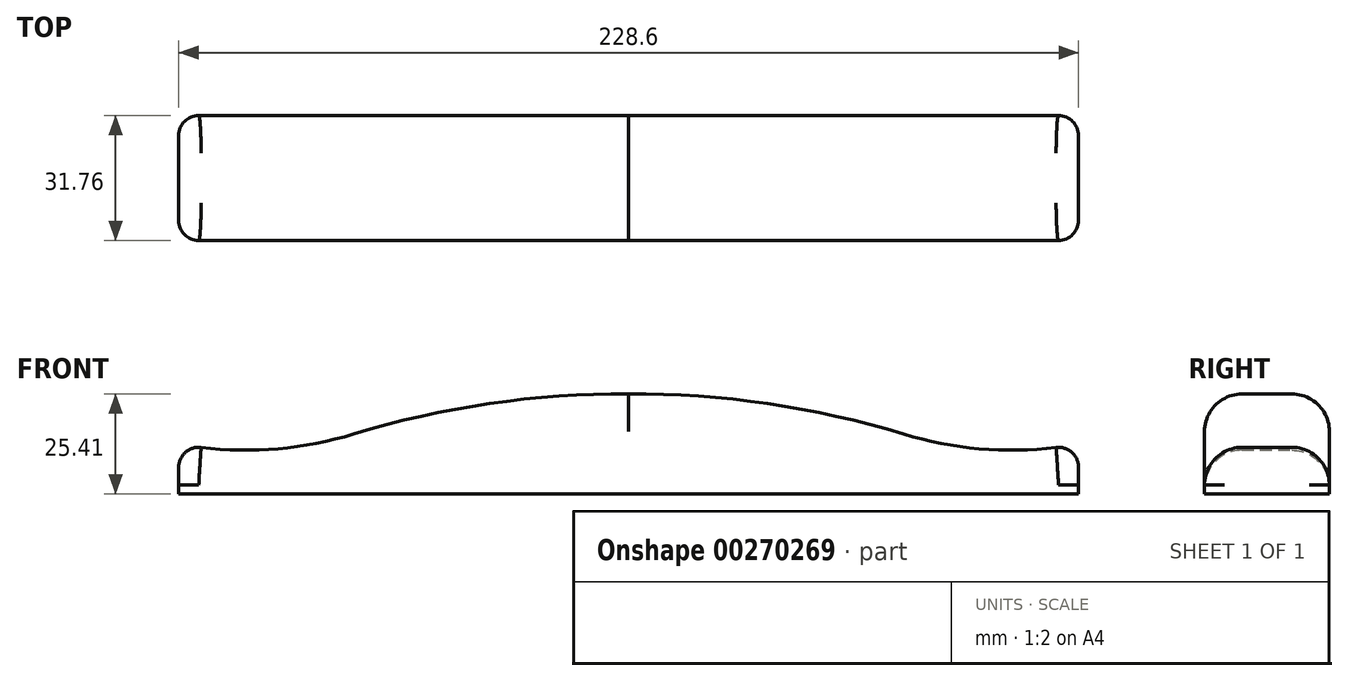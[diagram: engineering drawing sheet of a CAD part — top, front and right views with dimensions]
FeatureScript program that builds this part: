
annotation { "Feature Type Name" : "Feature", "Feature Type Description" : "" }
export const myFeature = defineFeature(function(context is Context, id is Id, definition is map)
    precondition{}
    {
        {
            var Q0;
            Q0=qCreatedBy(makeId("Front.planeOp"),FACE);
            var sketch = newSketch(context, id + "F0", { "sketchPlane" : qUnion([Q0])});
            skLineSegment(sketch, "E0", {"start": v(0, 0) * mm, "end": v(114.3, 0) * mm});
            skLineSegment(sketch, "E1", {"start": v(114.3, 0) * mm, "end": v(114.3, 12.7) * mm});
            skLineSegment(sketch, "E2", {"start": v(0, 0) * mm, "end": v(0, 25.4) * mm});
            skArc(sketch, "E3", {"start": v(69.85, 15.24) * mm, "mid": v(35.31, 22.98) * mm, "end": v(0, 25.4) * mm});
            skArc(sketch, "E4", {"start": v(69.85, 15.24) * mm, "mid": v(91.92, 11.3) * mm, "end": v(114.3, 12.7) * mm});
            skLineSegment(sketch, "E5.MirrorCS", {"start": v(0, 0) * mm, "end": v(-114.3, 0) * mm});
            skLineSegment(sketch, "E6.MirrorCS", {"start": v(-114.3, 0) * mm, "end": v(-114.3, 12.7) * mm});
            skArc(sketch, "E7.MirrorCS", {"start": v(-69.85, 15.24) * mm, "mid": v(-91.92, 11.3) * mm, "end": v(-114.3, 12.7) * mm});
            skArc(sketch, "E8.MirrorCS", {"start": v(-69.85, 15.24) * mm, "mid": v(-35.31, 22.98) * mm, "end": v(0, 25.4) * mm});
            skSolve(sketch);
        }
        {
            var Q0;
            Q0=makeQuery(id+"F0.imprint","IMPRINT",FACE,{"disambiguationData":[TD([[makeQuery(id+"F0.imprint","IMPRINT",EDGE,{"derivedFrom":sQuery(id+"F0.wireOp",EDGE,"E0")}),1.0]])]});
            var Q1;
            Q1=makeQuery(id+"F0.imprint","IMPRINT",FACE,{"disambiguationData":[TD([[makeQuery(id+"F0.imprint","IMPRINT",EDGE,{"derivedFrom":sQuery(id+"F0.wireOp",EDGE,"E5.MirrorCS")}),-1.0]])]});
            extrude(context, id + "F1", {"entities" : qUnion([Q0, Q1]), "endBound" : BoundingType.SYMMETRIC, "depth" : 31.75 * mm});
        }
        {
            var Q0;
            Q0=makeQuery(id+"F1.opExtrude","CAP_EDGE",EDGE,{"disambiguationData":[OSD([sQuery(id+"F0.wireOp",EDGE,"E8.MirrorCS")])],"isStart":false});
            var Q1;
            Q1=makeQuery(id+"F1.opExtrude","CAP_EDGE",EDGE,{"disambiguationData":[OSD([sQuery(id+"F0.wireOp",EDGE,"E8.MirrorCS")])],"isStart":true});
            fillet(context, id + "F2", {"entities" : qUnion([Q0, Q1]), "radius" : 9.52 * mm, "tangentPropagation" : true, "allowEdgeOverflow" : false});
        }
        {
            var Q0;
            Q0=makeQuery(id+"F1.opExtrude","SWEPT_EDGE",EDGE,{"disambiguationData":[OSD([sQuery(id+"F0.wireOp",EDGE,"E6.MirrorCS"),sQuery(id+"F0.wireOp",EDGE,"E7.MirrorCS")])]});
            var Q1;
            Q1=makeQuery(id+"F1.opExtrude","SWEPT_EDGE",EDGE,{"disambiguationData":[OSD([sQuery(id+"F0.wireOp",EDGE,"E1"),sQuery(id+"F0.wireOp",EDGE,"E4")])]});
            fillet(context, id + "F3", {"entities" : qUnion([Q0, Q1]), "radius" : 5.08 * mm, "tangentPropagation" : true, "allowEdgeOverflow" : false});
        }
    });
